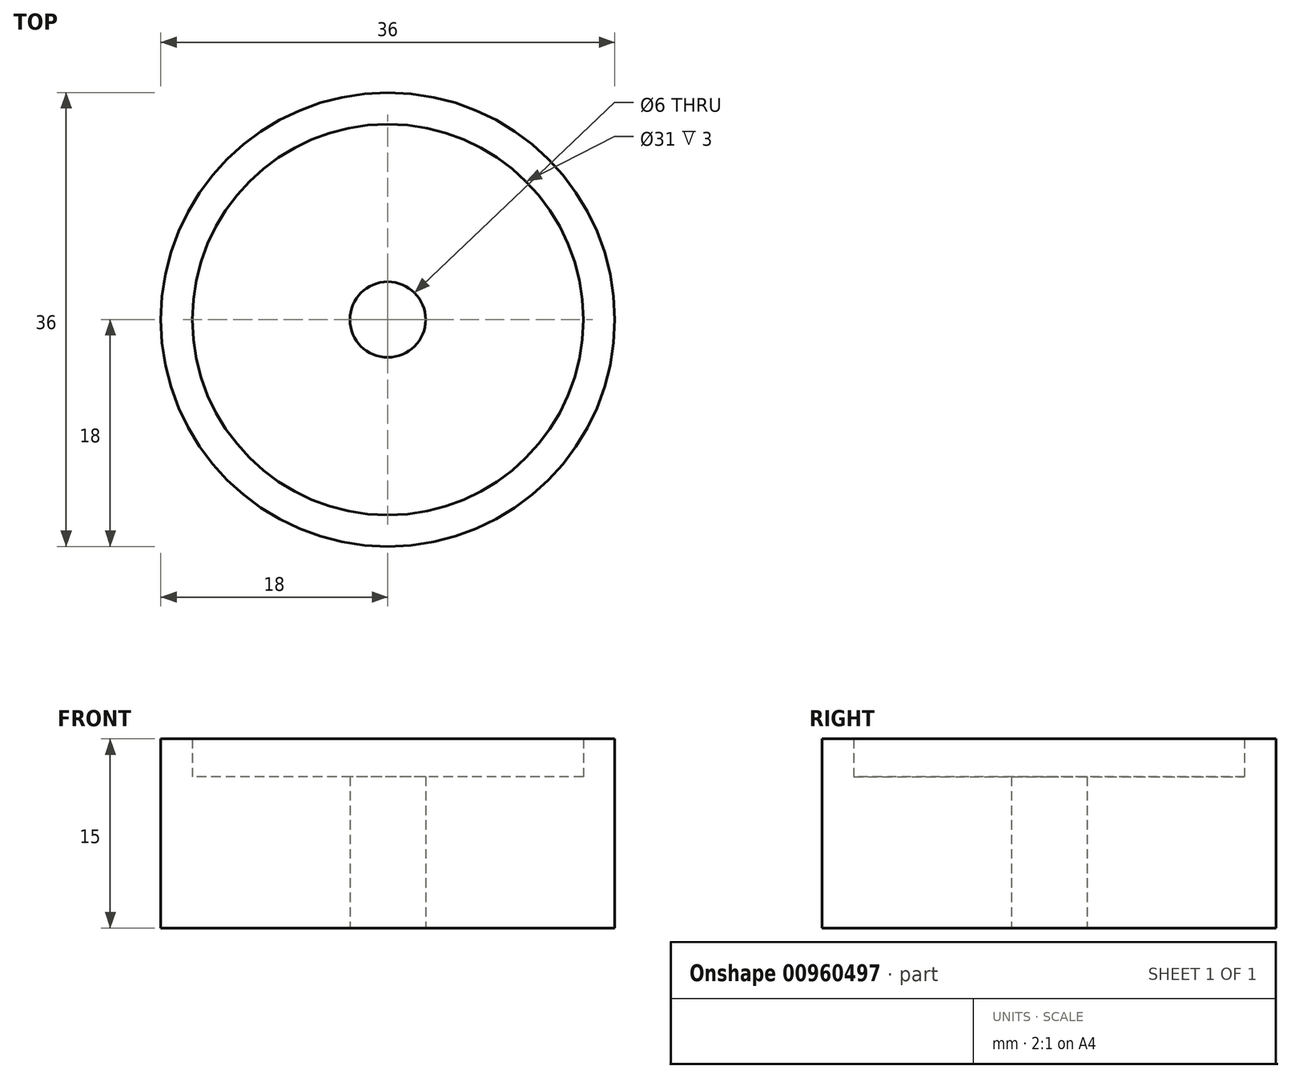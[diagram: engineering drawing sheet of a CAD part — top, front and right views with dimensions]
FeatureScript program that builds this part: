
annotation { "Feature Type Name" : "Feature", "Feature Type Description" : "" }
export const myFeature = defineFeature(function(context is Context, id is Id, definition is map)
    precondition{}
    {
        {
            var Q0;
            Q0=qCreatedBy(makeId("Top.planeOp"),FACE);
            var sketch = newSketch(context, id + "F0", { "sketchPlane" : qUnion([Q0])});
            skCircle(sketch, "E0", {"center": v(0, 0) * mm, "radius": 12.5 * mm});
            skCircle(sketch, "E1", {"center": v(0, 0) * mm, "radius": 15.5 * mm});
            skCircle(sketch, "E2", {"center": v(0, 0) * mm, "radius": 18 * mm});
            skCircle(sketch, "E3", {"center": v(0, 0) * mm, "radius": 3 * mm});
            skSolve(sketch);
        }
        {
            var Q0;
            {var subQ0=sQuery(id+"F0.wireOp",EDGE,"tqGnxmYz-Ac0E-lWUh-8vrP-u7RCHS2KXp5X");var subQ1=sQuery(id+"F0.wireOp",EDGE,"E0");var subQ2=makeQuery(id+"F0.imprint","INTERSECT",VERTEX,{"derivedFrom":[subQ1,subQ0]});Q0=makeQuery(id+"F0.imprint","IMPRINT",FACE,{"disambiguationData":[TD([[makeQuery(id+"F0.imprint","IMPRINT",EDGE,{"disambiguationData":[TD([[subQ2,1.0]])],"derivedFrom":subQ1}),-1.0]])]});}
            var Q1;
            Q1=makeQuery(id+"F0.imprint","IMPRINT",FACE,{"disambiguationData":[TD([[makeQuery(id+"F0.imprint","IMPRINT",EDGE,{"derivedFrom":sQuery(id+"F0.wireOp",EDGE,"E0")}),1.0]])]});
            extrude(context, id + "F1", {"entities" : qUnion([Q0, Q1]), "depth" : 12 * mm, "offsetDistance" : 25 * mm});
        }
        {
            var Q0;
            {var subQ0=sQuery(id+"F0.wireOp",EDGE,"tqGnxmYz-Ac0E-lWUh-8vrP-u7RCHS2KXp5X");var subQ1=sQuery(id+"F0.wireOp",EDGE,"E1");var subQ2=makeQuery(id+"F0.imprint","INTERSECT",VERTEX,{"derivedFrom":[subQ1,subQ0]});Q0=makeQuery(id+"F0.imprint","IMPRINT",FACE,{"disambiguationData":[TD([[makeQuery(id+"F0.imprint","IMPRINT",EDGE,{"disambiguationData":[TD([[subQ2,1.0]])],"derivedFrom":subQ1}),-1.0]])]});}
            extrude(context, id + "F2", {"entities" : qUnion([Q0]), "operationType" : NewBodyOperationType.ADD, "depth" : 15 * mm, "offsetDistance" : 25 * mm});
        }
    });
